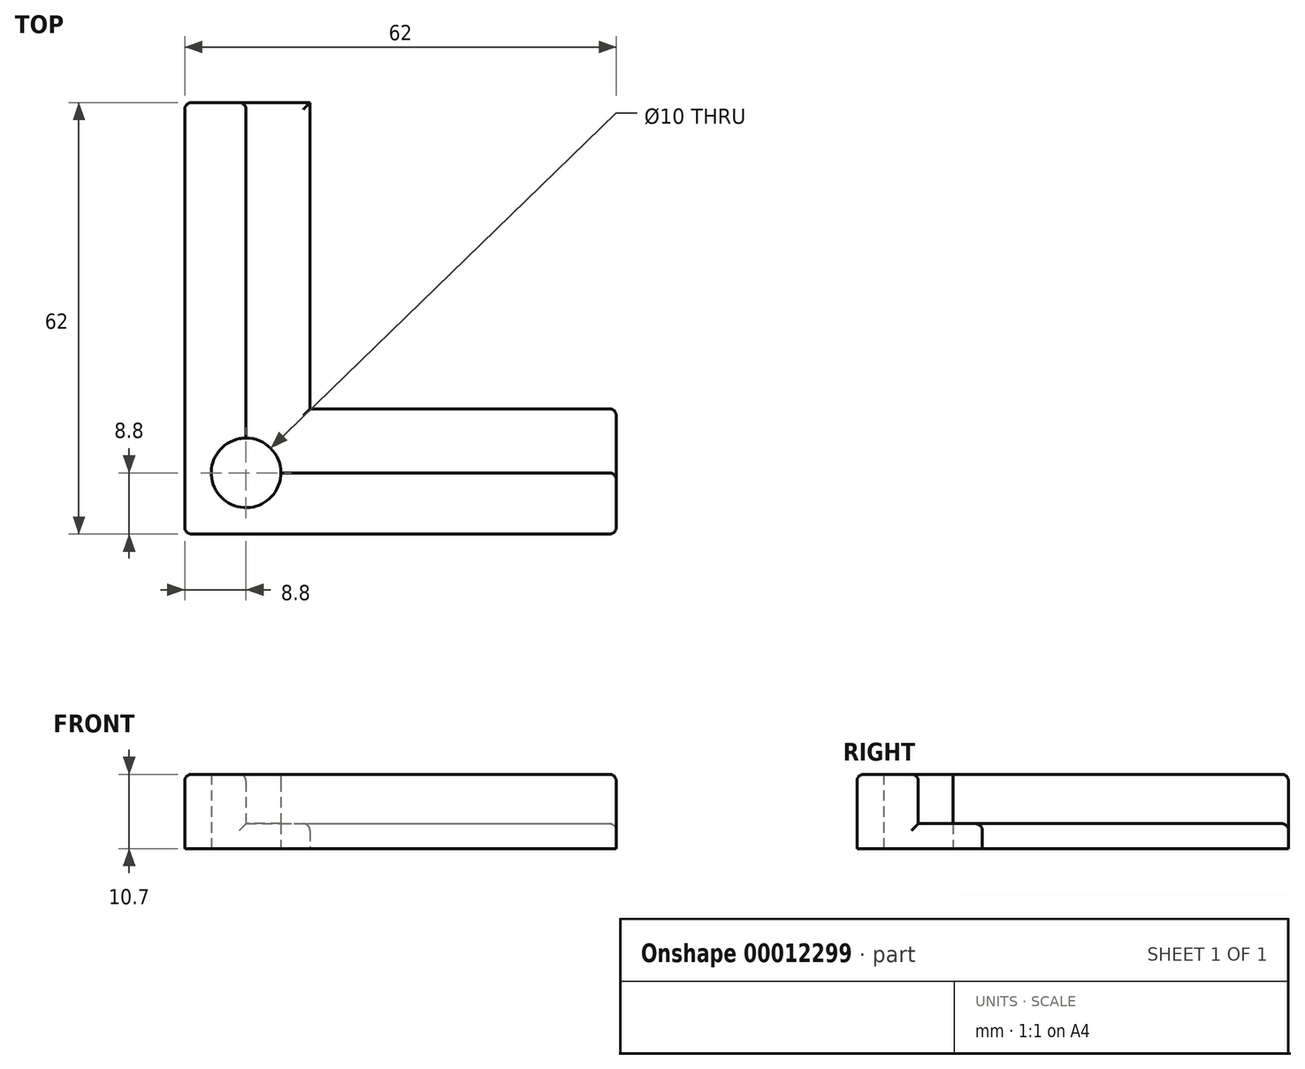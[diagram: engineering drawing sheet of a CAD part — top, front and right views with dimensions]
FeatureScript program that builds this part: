
annotation { "Feature Type Name" : "Feature", "Feature Type Description" : "" }
export const myFeature = defineFeature(function(context is Context, id is Id, definition is map)
    precondition{}
    {
        {
            var Q0;
            Q0=qCreatedBy(makeId("Top.planeOp"),FACE);
            var sketch = newSketch(context, id + "F0", { "sketchPlane" : qUnion([Q0])});
            skLineSegment(sketch, "E0", {"start": v(0, 0) * mm, "end": v(0, 62) * mm});
            skLineSegment(sketch, "E1", {"start": v(0, 62) * mm, "end": v(18, 62) * mm});
            skLineSegment(sketch, "E2", {"start": v(18, 62) * mm, "end": v(18, 18) * mm});
            skLineSegment(sketch, "E3", {"start": v(18, 18) * mm, "end": v(62, 18) * mm});
            skLineSegment(sketch, "E4", {"start": v(62, 18) * mm, "end": v(62, 0) * mm});
            skLineSegment(sketch, "E5", {"start": v(62, 0) * mm, "end": v(0, 0) * mm});
            skLineSegment(sketch, "E6.bottom", {"start": v(0, 0) * mm, "end": v(8.8, 0) * mm, "construction": true});
            skLineSegment(sketch, "E6.left", {"start": v(0, 0) * mm, "end": v(0, 8.8) * mm, "construction": true});
            skCircle(sketch, "E7", {"center": v(8.8, 8.8) * mm, "radius": 5 * mm});
            skSolve(sketch);
        }
        {
            var Q0;
            Q0=makeQuery(id+"F0.imprint","IMPRINT",FACE,{"disambiguationData":[TD([[makeQuery(id+"F0.imprint","IMPRINT",EDGE,{"derivedFrom":sQuery(id+"F0.wireOp",EDGE,"E0")}),-1.0]])]});
            extrude(context, id + "F1", {"entities" : qUnion([Q0]), "depth" : 3.6 * mm});
        }
        {
            var Q0;
            Q0=makeQuery(id+"F1.opExtrude","CAP_FACE",FACE,{"disambiguationData":[OSD([sQuery(id+"F0.wireOp",EDGE,"E0"),sQuery(id+"F0.wireOp",EDGE,"E1"),sQuery(id+"F0.wireOp",EDGE,"E2"),sQuery(id+"F0.wireOp",EDGE,"E3"),sQuery(id+"F0.wireOp",EDGE,"E4"),sQuery(id+"F0.wireOp",EDGE,"E5")])],"isStart":false});
            var sketch = newSketch(context, id + "F2", { "sketchPlane" : qUnion([Q0])});
            skLineSegment(sketch, "E8", {"start": v(62, 0) * mm, "end": v(0, 0) * mm});
            skLineSegment(sketch, "E9", {"start": v(0, 0) * mm, "end": v(0, 62) * mm});
            skLineSegment(sketch, "E10", {"start": v(0, 62) * mm, "end": v(8.8, 62) * mm});
            skLineSegment(sketch, "E11", {"start": v(8.8, 62) * mm, "end": v(8.8, 8.8) * mm});
            skLineSegment(sketch, "E12", {"start": v(8.8, 8.8) * mm, "end": v(62, 8.8) * mm});
            skLineSegment(sketch, "E13", {"start": v(62, 8.8) * mm, "end": v(62, 0) * mm});
            skSolve(sketch);
        }
        {
            var Q0;
            Q0=makeQuery(id+"F2.imprint","IMPRINT",FACE,{"disambiguationData":[TD([[makeQuery(id+"F2.imprint","IMPRINT",EDGE,{"derivedFrom":sQuery(id+"F2.wireOp",EDGE,"E8")}),-1.0]])]});
            extrude(context, id + "F3", {"entities" : qUnion([Q0]), "operationType" : NewBodyOperationType.ADD, "depth" : 7.1 * mm});
        }
        {
            var Q0;
            Q0=makeQuery(id+"F3.boolean.opBoolean","MERGE",EDGE,{"derivedFrom":[makeQuery(id+"F1.opExtrude","SWEPT_EDGE",EDGE,{"disambiguationData":[OSD([sQuery(id+"F0.wireOp",EDGE,"E0"),sQuery(id+"F0.wireOp",EDGE,"E5")])]}),makeQuery(id+"F3.opExtrude","SWEPT_EDGE",EDGE,{"disambiguationData":[OSD([sQuery(id+"F2.wireOp",EDGE,"E8"),sQuery(id+"F2.wireOp",EDGE,"E9")])]})]});
            var Q1;
            Q1=makeQuery(id+"F3.opExtrude","CAP_EDGE",EDGE,{"disambiguationData":[OSD([sQuery(id+"F2.wireOp",EDGE,"E8")])],"isStart":false});
            var Q2;
            Q2=makeQuery(id+"F3.opExtrude","CAP_EDGE",EDGE,{"disambiguationData":[OSD([sQuery(id+"F2.wireOp",EDGE,"E12")])],"isStart":false});
            var Q3;
            Q3=makeQuery(id+"F3.opExtrude","CAP_EDGE",EDGE,{"disambiguationData":[OSD([sQuery(id+"F2.wireOp",EDGE,"E11")])],"isStart":false});
            var Q4;
            Q4=makeQuery(id+"F3.opExtrude","CAP_EDGE",EDGE,{"disambiguationData":[OSD([sQuery(id+"F2.wireOp",EDGE,"E9")])],"isStart":false});
            var Q5;
            Q5=makeQuery(id+"F3.opExtrude","CAP_EDGE",EDGE,{"disambiguationData":[OSD([sQuery(id+"F2.wireOp",EDGE,"E10")])],"isStart":false});
            var Q6;
            Q6=makeQuery(id+"F3.opExtrude","CAP_EDGE",EDGE,{"disambiguationData":[OSD([sQuery(id+"F2.wireOp",EDGE,"E13")])],"isStart":false});
            var Q7;
            Q7=makeQuery(id+"F3.boolean.opBoolean","MERGE",EDGE,{"derivedFrom":[makeQuery(id+"F1.opExtrude","SWEPT_EDGE",EDGE,{"disambiguationData":[OSD([sQuery(id+"F0.wireOp",EDGE,"E4"),sQuery(id+"F0.wireOp",EDGE,"E5")])]}),makeQuery(id+"F3.opExtrude","SWEPT_EDGE",EDGE,{"disambiguationData":[OSD([sQuery(id+"F2.wireOp",EDGE,"E8"),sQuery(id+"F2.wireOp",EDGE,"E13")])]})]});
            var Q8;
            Q8=makeQuery(id+"F1.opExtrude","SWEPT_EDGE",EDGE,{"disambiguationData":[OSD([sQuery(id+"F0.wireOp",EDGE,"E3"),sQuery(id+"F0.wireOp",EDGE,"E4")])]});
            var Q9;
            Q9=makeQuery(id+"F1.opExtrude","CAP_EDGE",EDGE,{"disambiguationData":[OSD([sQuery(id+"F0.wireOp",EDGE,"E4")])],"isStart":false});
            var Q10;
            Q10=makeQuery(id+"F3.opExtrude","SWEPT_EDGE",EDGE,{"disambiguationData":[OSD([sQuery(id+"F0.wireOp",EDGE,"E4"),sQuery(id+"F2.wireOp",EDGE,"E12"),sQuery(id+"F2.wireOp",EDGE,"E13")])]});
            var Q11;
            Q11=makeQuery(id+"F1.opExtrude","CAP_EDGE",EDGE,{"disambiguationData":[OSD([sQuery(id+"F0.wireOp",EDGE,"E2")])],"isStart":false});
            var Q12;
            Q12=makeQuery(id+"F1.opExtrude","CAP_EDGE",EDGE,{"disambiguationData":[OSD([sQuery(id+"F0.wireOp",EDGE,"E3")])],"isStart":false});
            var Q13;
            Q13=makeQuery(id+"F1.opExtrude","CAP_EDGE",EDGE,{"disambiguationData":[OSD([sQuery(id+"F0.wireOp",EDGE,"E1")])],"isStart":false});
            var Q14;
            Q14=makeQuery(id+"F3.opExtrude","SWEPT_EDGE",EDGE,{"disambiguationData":[OSD([sQuery(id+"F0.wireOp",EDGE,"E1"),sQuery(id+"F2.wireOp",EDGE,"E10"),sQuery(id+"F2.wireOp",EDGE,"E11")])]});
            var Q15;
            Q15=makeQuery(id+"F3.boolean.opBoolean","MERGE",EDGE,{"derivedFrom":[makeQuery(id+"F1.opExtrude","SWEPT_EDGE",EDGE,{"disambiguationData":[OSD([sQuery(id+"F0.wireOp",EDGE,"E0"),sQuery(id+"F0.wireOp",EDGE,"E1")])]}),makeQuery(id+"F3.opExtrude","SWEPT_EDGE",EDGE,{"disambiguationData":[OSD([sQuery(id+"F2.wireOp",EDGE,"E9"),sQuery(id+"F2.wireOp",EDGE,"E10")])]})]});
            fillet(context, id + "F4", {"entities" : qUnion([Q0, Q1, Q2, Q3, Q4, Q5, Q6, Q7, Q8, Q9, Q10, Q11, Q12, Q13, Q14, Q15]), "radius" : 1 * mm, "tangentPropagation" : true, "allowEdgeOverflow" : false});
        }
    });
